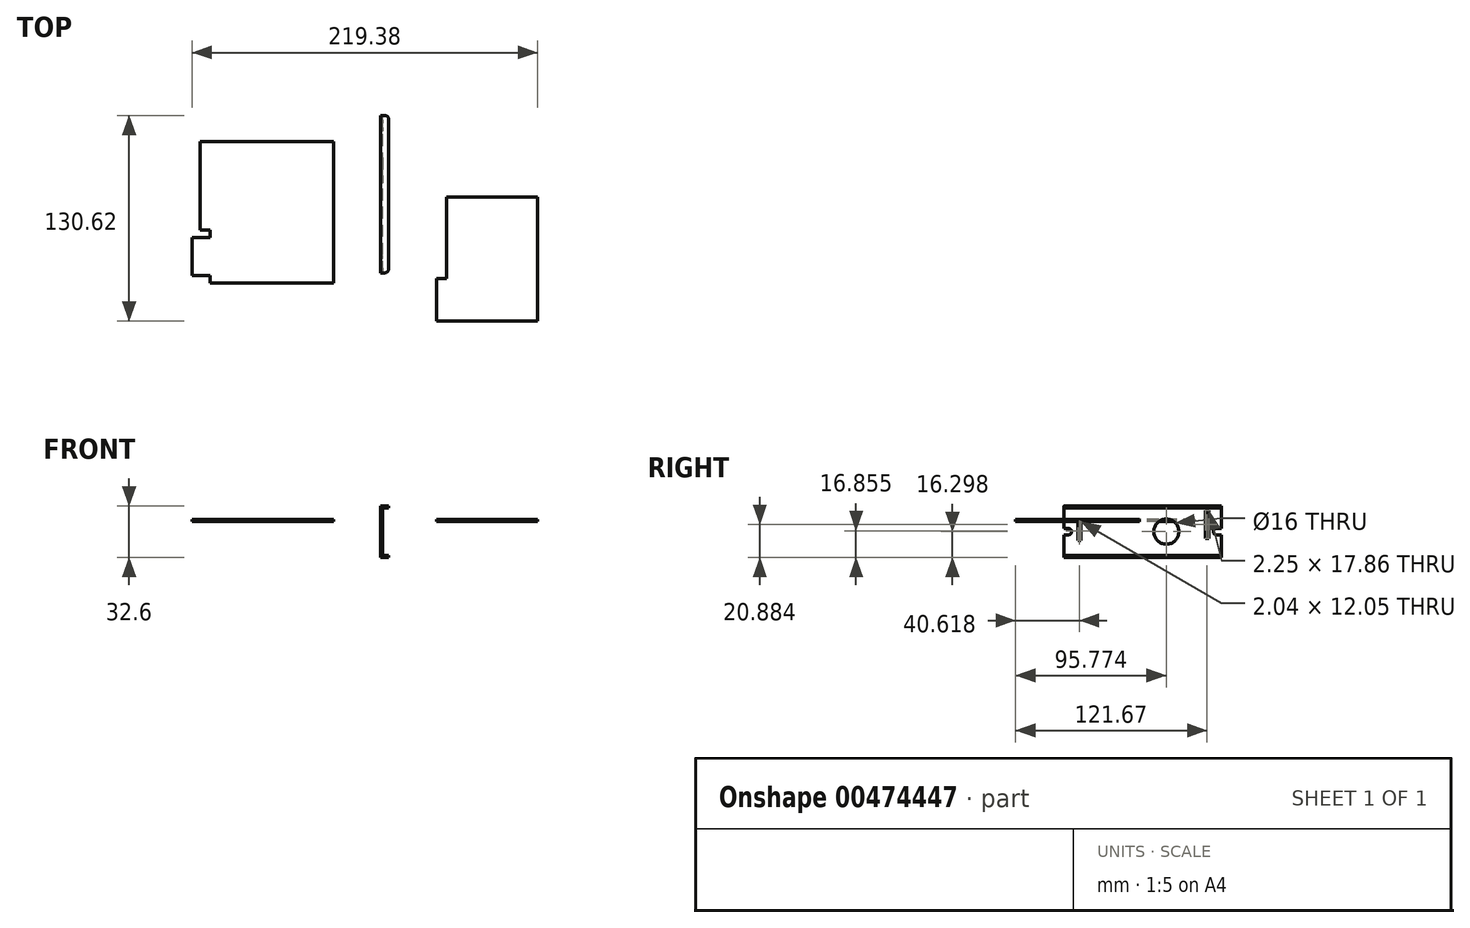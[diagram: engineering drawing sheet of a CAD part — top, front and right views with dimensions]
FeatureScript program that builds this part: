
annotation { "Feature Type Name" : "Feature", "Feature Type Description" : "" }
export const myFeature = defineFeature(function(context is Context, id is Id, definition is map)
    precondition{}
    {
        {
            var Q0;
            Q0=qCreatedBy(makeId("Right.planeOp"),FACE);
            var sketch = newSketch(context, id + "F0", { "sketchPlane" : qUnion([Q0])});
            skLineSegment(sketch, "E0.bottom", {"start": v(-12.04, 8.42) * mm, "end": v(87.96, 8.42) * mm});
            skLineSegment(sketch, "E0.top", {"start": v(-12.04, -21.58) * mm, "end": v(87.96, -21.58) * mm});
            skLineSegment(sketch, "E0.left", {"start": v(-12.04, 8.42) * mm, "end": v(-12.04, -4.58) * mm});
            skLineSegment(sketch, "E0.right", {"start": v(87.96, 8.42) * mm, "end": v(87.96, -4.58) * mm});
            skCircle(sketch, "E1", {"center": v(53.11, -6.58) * mm, "radius": 8 * mm});
            skLineSegment(sketch, "E2.bottom", {"start": v(-9.02, -8.58) * mm, "end": v(-12.04, -8.58) * mm});
            skLineSegment(sketch, "E2.top", {"start": v(-9.02, -4.58) * mm, "end": v(-12.04, -4.58) * mm});
            skArc(sketch, "E3", {"start": v(-9.02, -8.58) * mm, "mid": v(-7.02, -6.58) * mm, "end": v(-9.02, -4.58) * mm});
            skLineSegment(sketch, "E4.trimOffspring", {"start": v(-12.04, -8.58) * mm, "end": v(-12.04, -21.58) * mm});
            skLineSegment(sketch, "E5.bottom", {"start": v(84.94, -4.58) * mm, "end": v(87.96, -4.58) * mm});
            skLineSegment(sketch, "E5.top", {"start": v(84.94, -8.58) * mm, "end": v(87.96, -8.58) * mm});
            skArc(sketch, "E6", {"start": v(84.94, -4.58) * mm, "mid": v(82.94, -6.58) * mm, "end": v(84.94, -8.58) * mm});
            skLineSegment(sketch, "E7.trimOffspring", {"start": v(87.96, -8.58) * mm, "end": v(87.96, -21.58) * mm});
            skLineSegment(sketch, "E8.bottom", {"start": v(-3.06, 0) * mm, "end": v(-1.02, 0) * mm});
            skLineSegment(sketch, "E8.top", {"start": v(-3.06, -12.05) * mm, "end": v(-1.02, -12.05) * mm});
            skLineSegment(sketch, "E8.left", {"start": v(-3.06, 0) * mm, "end": v(-3.06, -12.05) * mm});
            skLineSegment(sketch, "E8.right", {"start": v(-1.02, 0) * mm, "end": v(-1.02, -12.05) * mm});
            skLineSegment(sketch, "E9.bottom", {"start": v(80.13, 6.94) * mm, "end": v(77.89, 6.94) * mm});
            skLineSegment(sketch, "E9.top", {"start": v(80.13, -10.93) * mm, "end": v(77.89, -10.93) * mm});
            skLineSegment(sketch, "E9.left", {"start": v(80.13, 6.94) * mm, "end": v(80.13, -10.93) * mm});
            skLineSegment(sketch, "E9.right", {"start": v(77.89, 6.94) * mm, "end": v(77.89, -10.93) * mm});
            skSolve(sketch);
        }
        {
            var Q0;
            Q0=makeQuery(id+"F0.imprint","IMPRINT",FACE,{"disambiguationData":[TD([[makeQuery(id+"F0.imprint","IMPRINT",EDGE,{"derivedFrom":sQuery(id+"F0.wireOp",EDGE,"E0.bottom")}),-1.0]])]});
            extrude(context, id + "F1", {"entities" : qUnion([Q0]), "depth" : 1.2 * mm});
        }
        {
            var Q0;
            Q0=makeQuery(id+"F1.opExtrude","CAP_FACE",FACE,{"disambiguationData":[OSD([sQuery(id+"F0.wireOp",EDGE,"E0.bottom"),sQuery(id+"F0.wireOp",EDGE,"E0.top"),sQuery(id+"F0.wireOp",EDGE,"E0.left"),sQuery(id+"F0.wireOp",EDGE,"E0.right"),sQuery(id+"F0.wireOp",EDGE,"E1"),sQuery(id+"F0.wireOp",EDGE,"E2.bottom"),sQuery(id+"F0.wireOp",EDGE,"E2.top"),sQuery(id+"F0.wireOp",EDGE,"E3"),sQuery(id+"F0.wireOp",EDGE,"E4.trimOffspring"),sQuery(id+"F0.wireOp",EDGE,"E5.bottom"),sQuery(id+"F0.wireOp",EDGE,"E5.top"),sQuery(id+"F0.wireOp",EDGE,"E6"),sQuery(id+"F0.wireOp",EDGE,"E7.trimOffspring"),sQuery(id+"F0.wireOp",EDGE,"E8.bottom"),sQuery(id+"F0.wireOp",EDGE,"E8.top"),sQuery(id+"F0.wireOp",EDGE,"E8.left"),sQuery(id+"F0.wireOp",EDGE,"E8.right"),sQuery(id+"F0.wireOp",EDGE,"E9.bottom"),sQuery(id+"F0.wireOp",EDGE,"E9.top"),sQuery(id+"F0.wireOp",EDGE,"E9.left"),sQuery(id+"F0.wireOp",EDGE,"E9.right")])],"isStart":true});
            var sketch = newSketch(context, id + "F2", { "sketchPlane" : qUnion([Q0])});
            skLineSegment(sketch, "E10.0", {"start": v(12.04, 8.42) * mm, "end": v(-87.96, 8.42) * mm});
            skLineSegment(sketch, "E10.1", {"start": v(-87.96, 8.42) * mm, "end": v(-87.96, 9.72) * mm});
            skLineSegment(sketch, "E10.2", {"start": v(12.04, 9.72) * mm, "end": v(-87.96, 9.72) * mm});
            skLineSegment(sketch, "E10.3", {"start": v(12.04, 8.42) * mm, "end": v(12.04, 9.72) * mm});
            skSolve(sketch);
        }
        {
            var Q0;
            Q0=makeQuery(id+"F2.imprint","IMPRINT",FACE,{"disambiguationData":[TD([[makeQuery(id+"F2.imprint","IMPRINT",EDGE,{"derivedFrom":sQuery(id+"F2.wireOp",EDGE,"E10.0")}),-1.0]])]});
            extrude(context, id + "F3", {"entities" : qUnion([Q0]), "operationType" : NewBodyOperationType.ADD, "oppositeDirection" : true, "depth" : 5 * mm});
        }
        {
            var Q0;
            Q0=makeQuery(id+"F3.boolean.opBoolean","MERGE",FACE,{"derivedFrom":[makeQuery(id+"F1.opExtrude","CAP_FACE",FACE,{"disambiguationData":[OSD([sQuery(id+"F0.wireOp",EDGE,"E0.bottom"),sQuery(id+"F0.wireOp",EDGE,"E0.top"),sQuery(id+"F0.wireOp",EDGE,"E0.left"),sQuery(id+"F0.wireOp",EDGE,"E0.right"),sQuery(id+"F0.wireOp",EDGE,"E1"),sQuery(id+"F0.wireOp",EDGE,"E2.bottom"),sQuery(id+"F0.wireOp",EDGE,"E2.top"),sQuery(id+"F0.wireOp",EDGE,"E3"),sQuery(id+"F0.wireOp",EDGE,"E4.trimOffspring"),sQuery(id+"F0.wireOp",EDGE,"E5.bottom"),sQuery(id+"F0.wireOp",EDGE,"E5.top"),sQuery(id+"F0.wireOp",EDGE,"E6"),sQuery(id+"F0.wireOp",EDGE,"E7.trimOffspring"),sQuery(id+"F0.wireOp",EDGE,"E8.bottom"),sQuery(id+"F0.wireOp",EDGE,"E8.top"),sQuery(id+"F0.wireOp",EDGE,"E8.left"),sQuery(id+"F0.wireOp",EDGE,"E8.right"),sQuery(id+"F0.wireOp",EDGE,"E9.bottom"),sQuery(id+"F0.wireOp",EDGE,"E9.top"),sQuery(id+"F0.wireOp",EDGE,"E9.left"),sQuery(id+"F0.wireOp",EDGE,"E9.right")])],"isStart":true}),makeQuery(id+"F3.opExtrude","CAP_FACE",FACE,{"disambiguationData":[OSD([sQuery(id+"F2.wireOp",EDGE,"E10.0"),sQuery(id+"F2.wireOp",EDGE,"E10.1"),sQuery(id+"F2.wireOp",EDGE,"E10.2"),sQuery(id+"F2.wireOp",EDGE,"E10.3")])],"isStart":true})]});
            var sketch = newSketch(context, id + "F4", { "sketchPlane" : qUnion([Q0])});
            skLineSegment(sketch, "E11.bottom", {"start": v(12.04, -21.58) * mm, "end": v(-87.96, -21.58) * mm});
            skLineSegment(sketch, "E11.top", {"start": v(12.04, -22.88) * mm, "end": v(-87.96, -22.88) * mm});
            skLineSegment(sketch, "E11.left", {"start": v(12.04, -21.58) * mm, "end": v(12.04, -22.88) * mm});
            skLineSegment(sketch, "E11.right", {"start": v(-87.96, -21.58) * mm, "end": v(-87.96, -22.88) * mm});
            skSolve(sketch);
        }
        {
            var Q0;
            Q0 = qSketchRegion(id + "F4", true);
            extrude(context, id + "F5", {"entities" : qUnion([Q0]), "operationType" : NewBodyOperationType.ADD, "oppositeDirection" : true, "depth" : 5 * mm});
        }
        {
            var Q0;
            Q0=makeQuery(id+"F3.opExtrude","CAP_EDGE",EDGE,{"disambiguationData":[OSD([sQuery(id+"F2.wireOp",EDGE,"E10.3")])],"isStart":false});
            var Q1;
            Q1=makeQuery(id+"F3.opExtrude","CAP_EDGE",EDGE,{"disambiguationData":[OSD([sQuery(id+"F2.wireOp",EDGE,"E10.1")])],"isStart":false});
            var Q2;
            Q2=makeQuery(id+"F5.opExtrude","CAP_EDGE",EDGE,{"disambiguationData":[OSD([sQuery(id+"F4.wireOp",EDGE,"E11.right")])],"isStart":false});
            var Q3;
            Q3=makeQuery(id+"F5.opExtrude","CAP_EDGE",EDGE,{"disambiguationData":[OSD([sQuery(id+"F4.wireOp",EDGE,"E11.left")])],"isStart":false});
            fillet(context, id + "F6", {"entities" : qUnion([Q0, Q1, Q2, Q3]), "radius" : 2.5 * mm, "tangentPropagation" : true, "allowEdgeOverflow" : false});
        }
        {
            var Q0;
            Q0=qCreatedBy(makeId("Top.planeOp"),FACE);
            var sketch = newSketch(context, id + "F7", { "sketchPlane" : qUnion([Q0])});
            skLineSegment(sketch, "E12.bottom", {"start": v(-114.78, 71.35) * mm, "end": v(-29.78, 71.35) * mm});
            skLineSegment(sketch, "E12.top", {"start": v(-108.38, -18.65) * mm, "end": v(-29.78, -18.65) * mm});
            skLineSegment(sketch, "E12.left", {"start": v(-119.78, 10.25) * mm, "end": v(-119.78, -13.65) * mm});
            skLineSegment(sketch, "E12.right", {"start": v(-29.78, 71.35) * mm, "end": v(-29.78, -18.65) * mm});
            skLineSegment(sketch, "E13.0", {"start": v(-114.78, 71.35) * mm, "end": v(-114.78, 15.25) * mm});
            skLineSegment(sketch, "E14.0", {"start": v(-119.78, -13.65) * mm, "end": v(-108.38, -13.65) * mm});
            skLineSegment(sketch, "E15.0", {"start": v(-119.78, 10.25) * mm, "end": v(-108.38, 10.25) * mm});
            skLineSegment(sketch, "E16.0", {"start": v(-114.78, 15.25) * mm, "end": v(-108.38, 15.25) * mm});
            skLineSegment(sketch, "E17.0", {"start": v(-108.38, 15.25) * mm, "end": v(-108.38, 10.25) * mm});
            skLineSegment(sketch, "E18.trimOffspring", {"start": v(-108.38, -13.65) * mm, "end": v(-108.38, -18.65) * mm});
            skSolve(sketch);
        }
        {
            var Q0;
            Q0=qCreatedBy(makeId("Top.planeOp"),FACE);
            var sketch = newSketch(context, id + "F8", { "sketchPlane" : qUnion([Q0])});
            skLineSegment(sketch, "E19.0.3", {"start": v(35.56, -42.66) * mm, "end": v(99.6, -42.66) * mm});
            skLineSegment(sketch, "E19.0.4", {"start": v(99.6, -42.66) * mm, "end": v(99.6, 35.93) * mm});
            skLineSegment(sketch, "E19.0.5", {"start": v(99.6, 35.93) * mm, "end": v(41.67, 35.93) * mm});
            skLineSegment(sketch, "E20.0", {"start": v(35.56, -42.66) * mm, "end": v(35.56, -15.75) * mm});
            skLineSegment(sketch, "E21.0", {"start": v(41.67, -15.75) * mm, "end": v(41.67, 35.93) * mm});
            skLineSegment(sketch, "E22.0", {"start": v(35.56, -15.75) * mm, "end": v(41.67, -15.75) * mm});
            skSolve(sketch);
        }
        {
            var Q0;
            Q0=makeQuery(id+"F7.imprint","IMPRINT",FACE,{"disambiguationData":[TD([[makeQuery(id+"F7.imprint","IMPRINT",EDGE,{"derivedFrom":sQuery(id+"F7.wireOp",EDGE,"E12.bottom")}),-1.0]])]});
            var Q1;
            Q1=makeQuery(id+"F8.imprint","IMPRINT",FACE,{"disambiguationData":[TD([[makeQuery(id+"F8.imprint","IMPRINT",EDGE,{"derivedFrom":sQuery(id+"F8.wireOp",EDGE,"E19.0.3")}),1.0]])]});
            extrude(context, id + "F9", {"entities" : qUnion([Q0, Q1]), "depth" : 1.2 * mm});
        }
    });
